MODEL slx_0a711875c262
CONFIG AbsTol = auto
CONFIG EnableMultiTasking = off
CONFIG FixedStep = 0.00001
CONFIG InitFcn = T = 0.0001;
VBUS = 311;

Ld = 0.00525;
Lq = 0.012;
Rs = 0.958;


Wc = 1000;
Ws = 8;

W_b = 2000;

CONFIG MaxStep = auto
CONFIG MinStep = auto
CONFIG RelTol = 1e-3
CONFIG SampleTimeConstraint = Unconstrained
CONFIG SolverName = FixedStepAuto
CONFIG StartTime = 0.0
CONFIG StopTime = 5
BLOCK [SubSystem] Anti_Park
BLOCK [Fcn] Anti_Park/Fcn
  Expr = cos(u[1])*u[2]-sin(u[1])*u[3]
BLOCK [Fcn] Anti_Park/Fcn1
  Expr = sin(u[1])*u[2]+cos(u[1])*u[3]
BLOCK [Mux] Anti_Park/Mux1
  DisplayOption = bar
  Inputs = 3
BLOCK [Outport] Anti_Park/Ualpha
BLOCK [Outport] Anti_Park/Ubeta
  Port = 2
BLOCK [Inport] Anti_Park/Vd
  Port = 2
BLOCK [Inport] Anti_Park/Vq
BLOCK [Inport] Anti_Park/angle
  Port = 3
BLOCK [SubSystem] CLARKE
BLOCK [Inport] CLARKE/A
BLOCK [Outport] CLARKE/Alpha
BLOCK [Inport] CLARKE/B
  Port = 2
BLOCK [Outport] CLARKE/Beta
  Port = 2
BLOCK [Inport] CLARKE/C
  Port = 3
BLOCK [Mux] CLARKE/Mux
  DisplayOption = bar
  Inputs = 3
BLOCK [Fcn] CLARKE/alpha
  Expr = (u(1)-0.5*(u(2)+u(3)))*2/3
BLOCK [Fcn] CLARKE/beta
  Expr = sqrt(3)/2*(u(2)-u(3))*2/3
BLOCK [Constant] Constant4
  Value = 0
BLOCK [Reference] DC  REF=spsDCVoltageSourceLib/DC Voltage Source
  LibrarySourceBlock = sps_lib/Sources/DC Voltage Source
  NameLocation = right
  SourceBlock = spsDCVoltageSourceLib/DC Voltage Source
  SourceType = DC Voltage Source
BLOCK [Demux] Demux
  Outputs = 3
BLOCK [From] From
  GotoTag = Them
  NameLocation = right
BLOCK [From] From1
  GotoTag = Wm
  NameLocation = right
BLOCK [From] From2
  GotoTag = Them
  NameLocation = top
BLOCK [From] From3
  GotoTag = Rad
  NameLocation = top
BLOCK [Gain] Gain
  Gain = 4
BLOCK [Goto] Goto
  GotoTag = Signal
BLOCK [Goto] Goto1
  GotoTag = Te
BLOCK [Goto] Goto2
  GotoTag = Them
BLOCK [Goto] Goto3
  GotoTag = Wm
BLOCK [Goto] Goto4
  GotoTag = Ialpha
BLOCK [Goto] Goto5
  GotoTag = Ibeta
BLOCK [Goto] Goto6
  GotoTag = Rad
BLOCK [Reference] Iq  REF=powerlib_extras/Discrete 
Control Blocks/Discrete
PI Controller
  NameLocation = top
  SourceBlock = powerlib_extras/Discrete 
Control Blocks/Discrete
PI Controller
  SourceType = Discrete PI Controller
BLOCK [SubSystem] Mux1
BLOCK [BusSelector] Mux1/Bus Selector
  OutputSignals = Stator current is_a (A),Stator current is_b (A),Stator current is_c (A)
BLOCK [BusSelector] Mux1/Bus Selector1
  OutputSignals = Rotor speed wm (rad/s),Rotor angle thetam (rad),Electromagnetic torque Te (N*m)
BLOCK [Outport] Mux1/Iabc
  Port = 3
BLOCK [Mux] Mux1/Mux
  DisplayOption = bar
  Inputs = 3
BLOCK [Outport] Mux1/Te
BLOCK [Outport] Mux1/Them
  Port = 2
BLOCK [Outport] Mux1/Wm
  Port = 4
BLOCK [Inport] Mux1/m
BLOCK [SubSystem] PARK
BLOCK [Inport] PARK/Alpha
BLOCK [Inport] PARK/Beta
  Port = 2
BLOCK [Outport] PARK/D
BLOCK [Mux] PARK/Mux
  DisplayOption = bar
  Inputs = 3
BLOCK [Outport] PARK/Q
  Port = 2
BLOCK [Inport] PARK/The
  Port = 3
BLOCK [Fcn] PARK/d
  Expr = u(1)*cos(u(3))+u(2)*sin(u(3))
BLOCK [Fcn] PARK/q
  Expr = -u(1)*sin(u(3))+u(2)*cos(u(3))
BLOCK [Reference] Permanent Magnet Synchronous Machine1  REF=spsPermanentMagnetSynchronousMachineLib/Permanent Magnet
Synchronous Machine
  SourceBlock = spsPermanentMagnetSynchronousMachineLib/Permanent Magnet
Synchronous Machine
  SourceType = Permanent Magnet Synchronous Machine
BLOCK [SubSystem] SVPWM
BLOCK [CCaller] SVPWM/C Caller
  FunctionName = SVPWM
  PortSpecificationStruct = %)30     .    8 H   8    (     @         %    "     8    !     0         %  0 "0    $    _    07)G3F%M90  4&]R=$YA;64 4V-O<&4     26YD97@     5'EP90      4VEZ90      27-';&]B86P   X    P    !@    @    $          4    (     0    0    !         !  ! !60E53#@   #     &    "     0         !0    @    !    !     $         $  $ %9"55,.    .     8    (    !          %    "     $    %     0         0    !0...<+3154ch>
BLOCK [Constant] SVPWM/Constant2
  Value = VBUS
BLOCK [DataTypeConversion] SVPWM/Data Type Conversion
  OutDataTypeStr = double
  RndMeth = Floor
  SaturateOnIntegerOverflow = off
BLOCK [DataTypeConversion] SVPWM/Data Type Conversion1
  OutDataTypeStr = double
  RndMeth = Floor
  SaturateOnIntegerOverflow = off
BLOCK [DataTypeConversion] SVPWM/Data Type Conversion2
  OutDataTypeStr = double
  RndMeth = Floor
  SaturateOnIntegerOverflow = off
BLOCK [Logic] SVPWM/Logical Operator
  AllPortsSameDT = off
  Operator = NOT
  OutDataTypeStr = boolean
BLOCK [Logic] SVPWM/Logical Operator1
  AllPortsSameDT = off
  Operator = NOT
  OutDataTypeStr = boolean
BLOCK [Logic] SVPWM/Logical Operator2
  AllPortsSameDT = off
  Operator = NOT
  OutDataTypeStr = boolean
BLOCK [Mux] SVPWM/Mux
  DisplayOption = bar
  Inputs = 6
BLOCK [Reference] SVPWM/PWM Generator  REF=eePwmGenerator/PWM Generator
  LibrarySourceBlock = ee_sl_lib/Pulse Width
Modulation/PWM Generator
  SourceBlock = eePwmGenerator/PWM Generator
  SourceType = PWM Generator
BLOCK [Reference] SVPWM/PWM Generator1  REF=eePwmGenerator/PWM Generator
  LibrarySourceBlock = ee_sl_lib/Pulse Width
Modulation/PWM Generator
  SourceBlock = eePwmGenerator/PWM Generator
  SourceType = PWM Generator
BLOCK [Reference] SVPWM/PWM Generator2  REF=eePwmGenerator/PWM Generator
  LibrarySourceBlock = ee_sl_lib/Pulse Width
Modulation/PWM Generator
  SourceBlock = eePwmGenerator/PWM Generator
  SourceType = PWM Generator
BLOCK [Inport] SVPWM/Valpha
BLOCK [Inport] SVPWM/Vbeta
  Port = 2
BLOCK [ZeroOrderHold] SVPWM/Zero-Order Hold
  SampleTime = T
BLOCK [ZeroOrderHold] SVPWM/Zero-Order Hold1
  SampleTime = T
BLOCK [Outport] SVPWM/pulse
BLOCK [Scope] Scope
  ActiveDisplayYMaximum = 83.45959853190611
  ActiveDisplayYMinimum = 71.221659633413722
  ContainerLayout = {"WindowBounds":[213.33333333333326,149.33333333333326,1280,768],"gridDimensions":{"w":1,"h":1},"tileCount":1,"tileCoverage":1,"columnWeights":1,"rowWeights":1,"tileOccupancy":{}}
  Floating = off
  GraphicalSettings = {"Style":{"BackgroundColor":[0.12941176470588237,0.12941176470588237,0.12941176470588237],"AxesColor":[0.07058823529411765,0.07058823529411765,0.07058823529411765],"LabelsColor":[0.8509803921568627,0.8509803921568627,0.8509803921568627],"PreserveColors":false,"Visible":[true,true,true],"LineStyle":["-","-","-"],"LineWidth":[1.5,1.5,1.5],"BarWidth":[0.9,0.9,0.9],"LineColor":["auto","auto","auto"],"...<+2360ch>
  MultipleDisplayCache = [{"MaxYLimMag":432.50451314474628,"MaxYLimReal":83.45959853190611,"MinYLimMag":0,"MinYLimReal":71.221659633413722,"PlotAsMagnitudePhase":false,"ShowGrid":true,"ShowLegend":true,"Title":"%<SignalLabel>","YLabel":""}]
  NameLocation = right
  NumInputPorts = 3
  ScopeFrameLocation = window
  ShowLegend = on
  Visible = on
  WasSavedAsWebScope = on
  WindowPosition = [290.000000,171.000000,688.000000,501.000000,]
BLOCK [Scope] Scope1
  ActiveDisplayYMaximum = 56.919768702194638
  ActiveDisplayYMinimum = -56.765093426646764
  DataLoggingVariableName = ScopeData1
  Floating = off
  GraphicalSettings = {"Style":{"BackgroundColor":[0.12941176470588237,0.12941176470588237,0.12941176470588237],"AxesColor":[0.07058823529411765,0.07058823529411765,0.07058823529411765],"LabelsColor":[0.8509803921568627,0.8509803921568627,0.8509803921568627],"PreserveColors":false,"Visible":[true,true,true],"LineStyle":["-","-","-"],"LineWidth":[1.5,1.5,1.5],"BarWidth":[0.9,0.9,0.9],"LineColor":["auto","auto","auto"],"...<+2203ch>
  MultipleDisplayCache = [{"MaxYLimMag":56.919768702194638,"MaxYLimReal":56.919768702194638,"MinYLimMag":0,"MinYLimReal":-56.765093426646764,"PlotAsMagnitudePhase":false,"ShowGrid":true,"ShowLegend":false,"Title":"%<SignalLabel>","YLabel":""}]
  NumInputPorts = 3
  ScopeFrameLocation = window
  WasSavedAsWebScope = on
  WindowPosition = [420.000000,327.000000,560.000000,420.000000,]
BLOCK [Scope] Scope2
  ActiveDisplayYMaximum = 14.952214172172493
  ActiveDisplayYMinimum = -3.4308453898305751
  DataLoggingVariableName = ScopeData2
  Floating = off
  GraphicalSettings = {"Style":{"BackgroundColor":[0.12941176470588237,0.12941176470588237,0.12941176470588237],"AxesColor":[0.07058823529411765,0.07058823529411765,0.07058823529411765],"LabelsColor":[0.8509803921568627,0.8509803921568627,0.8509803921568627],"PreserveColors":false,"Visible":[true,true],"LineStyle":["-","-"],"LineWidth":[1.5,1.5],"BarWidth":[0.9,0.9],"LineColor":["auto","auto"],"LineFaceAlpha":[1,1],"Li...<+2100ch>
  MultipleDisplayCache = [{"MaxYLimMag":14.952214172172493,"MaxYLimReal":14.952214172172493,"MinYLimMag":0,"MinYLimReal":-3.4308453898305751,"PlotAsMagnitudePhase":false,"ShowGrid":true,"ShowLegend":false,"Title":"%<SignalLabel>","YLabel":""}]
  NumInputPorts = 2
  ScopeFrameLocation = window
  WasSavedAsWebScope = on
  WindowPosition = [420.000000,327.000000,560.000000,420.000000,]
BLOCK [Scope] Scope3
  ActiveDisplayYMaximum = 11.569758124701689
  ActiveDisplayYMinimum = -12.718687980408173
  ContainerLayout = {"WindowBounds":[213.33333333333326,149.33333333333326,1280,768],"gridDimensions":{"w":1,"h":1},"tileCount":1,"tileCoverage":1,"columnWeights":1,"rowWeights":1,"tileOccupancy":{}}
  DataLoggingVariableName = ScopeData3
  Floating = off
  GraphicalSettings = {"Style":{"BackgroundColor":[0.12941176470588237,0.12941176470588237,0.12941176470588237],"AxesColor":[0.07058823529411765,0.07058823529411765,0.07058823529411765],"LabelsColor":[0.8509803921568627,0.8509803921568627,0.8509803921568627],"PreserveColors":false,"Visible":[true,true],"LineStyle":["-","-"],"LineWidth":[1.5,1.5],"BarWidth":[0.9,0.9],"LineColor":["auto","auto"],"LineFaceAlpha":[1,1],"Li...<+2108ch>
  MultipleDisplayCache = [{"MaxYLimMag":16.784580665603098,"MaxYLimReal":11.569758124701689,"MinYLimMag":0,"MinYLimReal":-12.718687980408173,"PlotAsMagnitudePhase":false,"ShowGrid":true,"ShowLegend":true,"Title":"%<SignalLabel>","YLabel":""}]
  NumInputPorts = 2
  ScopeFrameLocation = window
  ShowLegend = on
  WasSavedAsWebScope = on
  WindowPosition = [577.000000,260.000000,560.000000,420.000000,]
BLOCK [Scope] Scope4
  ActiveDisplayYMaximum = 249.87801666414541
  ActiveDisplayYMinimum = -120.45590110912798
  ContainerLayout = {"WindowBounds":[213.33333333333326,149.33333333333326,1280,768],"gridDimensions":{"w":1,"h":1},"tileCount":1,"tileCoverage":1,"columnWeights":1,"rowWeights":1,"tileOccupancy":{}}
  DataLoggingVariableName = ScopeData4
  Floating = off
  GraphicalSettings = {"Style":{"BackgroundColor":[0.12941176470588237,0.12941176470588237,0.12941176470588237],"AxesColor":[0.07058823529411765,0.07058823529411765,0.07058823529411765],"LabelsColor":[0.8509803921568627,0.8509803921568627,0.8509803921568627],"PreserveColors":false,"Visible":[true,true],"LineStyle":["-","-"],"LineWidth":[1.5,1.5],"BarWidth":[0.9,0.9],"LineColor":["auto","auto"],"LineFaceAlpha":[1,1],"Li...<+2090ch>
  MultipleDisplayCache = [{"MaxYLimMag":15.588457268119896,"MaxYLimReal":249.87801666414541,"MinYLimMag":0,"MinYLimReal":-120.45590110912798,"PlotAsMagnitudePhase":false,"ShowGrid":true,"ShowLegend":true,"Title":"%<SignalLabel>","YLabel":""}]
  NumInputPorts = 2
  ScopeFrameLocation = window
  ShowLegend = on
  WasSavedAsWebScope = on
  WindowPosition = [696.000000,322.000000,560.000000,420.000000,]
BLOCK [Scope] Scope5
  ActiveDisplayYMaximum = 0.38689833522072209
  ActiveDisplayYMinimum = -2.417785617585527
  DataLoggingVariableName = ScopeData5
  Floating = off
  GraphicalSettings = {"Style":{"BackgroundColor":[0.12941176470588237,0.12941176470588237,0.12941176470588237],"AxesColor":[0.07058823529411765,0.07058823529411765,0.07058823529411765],"LabelsColor":[0.8509803921568627,0.8509803921568627,0.8509803921568627],"PreserveColors":false,"Visible":[true],"LineStyle":["-"],"LineWidth":[1.5],"BarWidth":[0.9],"LineColor":["auto"],"LineFaceAlpha":[1],"LineEdgeAlpha":[1],"Marker":...<+1895ch>
  MultipleDisplayCache = [{"MaxYLimMag":2.417785617585527,"MaxYLimReal":0.38689833522072209,"MinYLimMag":0,"MinYLimReal":-2.417785617585527,"PlotAsMagnitudePhase":false,"ShowGrid":true,"ShowLegend":false,"Title":"%<SignalLabel>","YLabel":""}]
  NumInputPorts = 1
  ScopeFrameLocation = window
  WasSavedAsWebScope = on
  WindowPosition = [573.000000,323.000000,560.000000,420.000000,]
BLOCK [Scope] Scope6
  ActiveDisplayYMaximum = 1828.1288182778874
  ActiveDisplayYMinimum = -6.298375426201801
  DataLoggingVariableName = ScopeData6
  Floating = off
  GraphicalSettings = {"AxesScalingProperties":{"AlignXAxis":"Center","AlignYAxis":"Center","AutoScaleXAxisLimits":false,"AxesScaling":"Manual","AxesScalingNumUpdates":10,"ExpandOnly":true,"ScaleAxesLimitsAtStop":false,"XAxisDataRange":100,"YAxisDataRange":80},"DisplayProperties":{"ColorOrder":["auto","auto","auto","auto","auto","auto","auto","auto","auto","auto","auto","auto","auto","auto","auto","auto","auto","auto",...<+2117ch>
  MultipleDisplayCache = [{"MaxYLimMag":1419.1346246899052,"MaxYLimReal":1828.1288182778874,"MinYLimMag":0,"MinYLimReal":-6.298375426201801,"PlotAsMagnitudePhase":false,"ShowGrid":true,"ShowLegend":true,"Title":"%<SignalLabel>","YLabel":""}]
  NumInputPorts = 2
  ScopeFrameLocation = window
  ShowLegend = on
  WasSavedAsWebScope = on
  WindowPosition = [656.000000,258.000000,560.000000,420.000000,]
BLOCK [Scope] Scope7
  ActiveDisplayYMaximum = 20.129691037464234
  ActiveDisplayYMinimum = 3.84321816794486
  DataLoggingVariableName = ScopeData7
  Floating = off
  GraphicalSettings = {"AxesScalingProperties":{"AlignXAxis":"Center","AlignYAxis":"Center","AutoScaleXAxisLimits":false,"AxesScaling":"Manual","AxesScalingNumUpdates":10,"ExpandOnly":true,"ScaleAxesLimitsAtStop":false,"XAxisDataRange":100,"YAxisDataRange":80},"DisplayProperties":{"ColorOrder":["auto","auto","auto","auto","auto","auto","auto","auto","auto","auto","auto","auto","auto","auto","auto","auto","auto","auto",...<+2119ch>
  MultipleDisplayCache = [{"MaxYLimMag":22.5,"MaxYLimReal":20.129691037464234,"MinYLimMag":0,"MinYLimReal":3.84321816794486,"PlotAsMagnitudePhase":false,"ShowGrid":true,"ShowLegend":true,"Title":"%<SignalLabel>","YLabel":""}]
  NumInputPorts = 2
  ScopeFrameLocation = window
  ShowLegend = on
  WasSavedAsWebScope = on
  WindowPosition = [656.000000,258.000000,560.000000,420.000000,]
BLOCK [Sum] Sum
  Inputs = |+-
BLOCK [Sum] Sum1
  Inputs = |+-
BLOCK [Sum] Sum2
  Inputs = |+-
BLOCK [Sum] Sum3
  Inputs = |+-
BLOCK [Step] TL
  SampleTime = 0
  Time = 3
BLOCK [SubSystem] Theta_Signal
BLOCK [Sum] Theta_Signal/Add
  IconShape = rectangular
BLOCK [Constant] Theta_Signal/Constant3
BLOCK [Gain] Theta_Signal/Gain
  Gain = pi
BLOCK [Reference] Theta_Signal/Sawtooth Generator  REF=spsSawtoothGeneratorLib/Sawtooth
Generator
  LibrarySourceBlock = sps_lib/Sources/Signal Generator Sources/Sawtooth
Generator
  SourceBlock = spsSawtoothGeneratorLib/Sawtooth
Generator
  SourceType = Sawtooth Generator
BLOCK [Outport] Theta_Signal/angle
BLOCK [TransferFcn] Transfer Fcn2
  Denominator = [1 sqrt(2)*Wc Wc^2]
  NameLocation = top
  Numerator = [Wc^2]
BLOCK [ZeroOrderHold] Zero-Order Hold
  NameLocation = right
  SampleTime = 0.0001
BLOCK [Reference] inverter  REF=spsUniversalBridgeLib/Universal Bridge
  LibrarySourceBlock = sps_lib/Power Electronics/Universal Bridge
  NameLocation = top
  SourceBlock = spsUniversalBridgeLib/Universal Bridge
  SourceType = Universal Bridge
BLOCK [Reference] ld  REF=powerlib_extras/Discrete 
Control Blocks/Discrete
PI Controller
  NameLocation = top
  SourceBlock = powerlib_extras/Discrete 
Control Blocks/Discrete
PI Controller
  SourceType = Discrete PI Controller
BLOCK [SubSystem] pi-Iq2
  AncestorBlock = powerlib_extras/Discrete 
Control Blocks/Discrete
PI Controller
  DialogController = POWERSYS.PowerSysDialog
BLOCK [DiscreteIntegrator] pi-Iq2/Discrete-Time Integrator
  ICPrevOutput = DiscIntNeverNeededParam
  ICPrevScaledInput = DiscIntNeverNeededParam
  InitialCondition = Init
  LimitOutput = on
  LowerSaturationLimit = LowerLimit
  SampleTime = Ts
  UpperSaturationLimit = UpperLimit
BLOCK [Inport] pi-Iq2/Error
  SampleTime = Ts
BLOCK [Gain] pi-Iq2/Kp4
  Gain = Kp
  OutDataTypeStr = Inherit: Same as input
  ParamDataTypeStr = Inherit: Same as input
  SampleTime = Ts
  SaturateOnIntegerOverflow = on
BLOCK [Gain] pi-Iq2/Kp5
  Gain = Ki
  OutDataTypeStr = Inherit: Same as input
  ParamDataTypeStr = Inherit: Same as input
  SampleTime = Ts
  SaturateOnIntegerOverflow = on
BLOCK [Outport] pi-Iq2/Out
  InitialOutput = 0
  SampleTime = Ts
BLOCK [Saturate] pi-Iq2/Saturation2
  LowerLimit = LowerLimit
  NameLocation = top
  SampleTime = Ts
  UpperLimit = UpperLimit
BLOCK [Sum] pi-Iq2/Sum6
  IconShape = rectangular
  InputSameDT = on
  OutDataTypeStr = Inherit: Same as first input
  SampleTime = Ts
  SaturateOnIntegerOverflow = on
BLOCK [ZeroOrderHold] pi-Iq2/Zero-Order Hold
  SampleTime = Ts
BLOCK [Reference] powergui  REF=spspowerguiLib/powergui
  SourceBlock = spspowerguiLib/powergui
  SourceType = PSB option menu block
BLOCK [Step] set
  After = 20
  NameLocation = top
  SampleTime = 0
  Time = 2
BLOCK [SubSystem] velocity1
  AncestorBlock = powerlib_extras/Discrete 
Control Blocks/Discrete
PI Controller
  DialogController = POWERSYS.PowerSysDialog
BLOCK [DiscreteIntegrator] velocity1/Discrete-Time Integrator
  ICPrevOutput = DiscIntNeverNeededParam
  ICPrevScaledInput = DiscIntNeverNeededParam
  InitialCondition = Init
  LimitOutput = on
  LowerSaturationLimit = LowerLimit
  SampleTime = Ts
  UpperSaturationLimit = UpperLimit
BLOCK [Inport] velocity1/Error
  SampleTime = Ts
BLOCK [Gain] velocity1/Kp4
  Gain = Kp
  OutDataTypeStr = Inherit: Same as input
  ParamDataTypeStr = Inherit: Same as input
  SampleTime = Ts
  SaturateOnIntegerOverflow = on
BLOCK [Gain] velocity1/Kp5
  Gain = Ki
  OutDataTypeStr = Inherit: Same as input
  ParamDataTypeStr = Inherit: Same as input
  SampleTime = Ts
  SaturateOnIntegerOverflow = on
BLOCK [Outport] velocity1/Out
  InitialOutput = 0
  SampleTime = Ts
BLOCK [Saturate] velocity1/Saturation2
  LowerLimit = LowerLimit
  NameLocation = top
  SampleTime = Ts
  UpperLimit = UpperLimit
BLOCK [Sum] velocity1/Sum6
  IconShape = rectangular
  InputSameDT = on
  OutDataTypeStr = Inherit: Same as first input
  SampleTime = Ts
  SaturateOnIntegerOverflow = on
BLOCK [ZeroOrderHold] velocity1/Zero-Order Hold
  SampleTime = Ts
BLOCK [Gain] wm->Nr
  Gain = 30/pi
  NameLocation = right
LINE Anti_Park/Fcn1:1 -> Anti_Park/Ubeta:1
LINE Anti_Park/Fcn:1 -> Anti_Park/Ualpha:1
LINE Anti_Park/Mux1:1 -> Anti_Park/Fcn1:1
LINE Anti_Park/Mux1:1 -> Anti_Park/Fcn:1
LINE Anti_Park/Vd:1 -> Anti_Park/Mux1:2
LINE Anti_Park/Vq:1 -> Anti_Park/Mux1:3
LINE Anti_Park/angle:1 -> Anti_Park/Mux1:1
LINE Anti_Park:1 -> SVPWM:1
LINE Anti_Park:2 -> SVPWM:2
LINE CLARKE/A:1 -> CLARKE/Mux:1
LINE CLARKE/B:1 -> CLARKE/Mux:2
LINE CLARKE/C:1 -> CLARKE/Mux:3
LINE CLARKE/Mux:1 -> CLARKE/alpha:1
LINE CLARKE/Mux:1 -> CLARKE/beta:1
LINE CLARKE/alpha:1 -> CLARKE/Alpha:1
LINE CLARKE/beta:1 -> CLARKE/Beta:1
LINE CLARKE:1 -> Goto4:1
LINE CLARKE:1 -> PARK:1
LINE CLARKE:1 -> Scope2:1
LINE CLARKE:2 -> Goto5:1
LINE CLARKE:2 -> PARK:2
LINE CLARKE:2 -> Scope2:2
LINE Constant4:1 -> Sum1:1
LINE DC:lconn -> inverter:rconn
LINE DC:rconn -> inverter:rconn
LINE Demux:1 -> CLARKE:1
LINE Demux:1 -> Scope1:1
LINE Demux:2 -> CLARKE:2
LINE Demux:2 -> Scope1:2
LINE Demux:3 -> CLARKE:3
LINE Demux:3 -> Scope1:3
LINE From1:1 -> wm->Nr:1
LINE From2:1 -> Anti_Park:3
LINE From2:1 -> Scope5:1
LINE From3:1 -> Scope7:2
LINE From3:1 -> Sum3:2
LINE From:1 -> PARK:3
LINE Gain:1 -> Goto2:1
LINE Iq:1 -> Anti_Park:1
LINE Iq:1 -> Scope4:1
LINE Mux1/Bus Selector1:1 -> Mux1/Wm:1
LINE Mux1/Bus Selector1:2 -> Mux1/Them:1
LINE Mux1/Bus Selector1:3 -> Mux1/Te:1
LINE Mux1/Bus Selector:1 -> Mux1/Mux:1
LINE Mux1/Bus Selector:2 -> Mux1/Mux:2
LINE Mux1/Bus Selector:3 -> Mux1/Mux:3
LINE Mux1/Mux:1 -> Mux1/Iabc:1
LINE Mux1/m:1 -> Mux1/Bus Selector1:1
LINE Mux1/m:1 -> Mux1/Bus Selector:1
LINE Mux1:1 -> Goto1:1
LINE Mux1:1 -> Scope:1
LINE Mux1:2 -> Gain:1
LINE Mux1:2 -> Goto6:1
LINE Mux1:2 -> Scope:2
LINE Mux1:3 -> Zero-Order Hold:1
LINE Mux1:4 -> Goto3:1
LINE Mux1:4 -> Scope:3
LINE PARK/Alpha:1 -> PARK/Mux:1
LINE PARK/Beta:1 -> PARK/Mux:2
LINE PARK/Mux:1 -> PARK/d:1
LINE PARK/Mux:1 -> PARK/q:1
LINE PARK/The:1 -> PARK/Mux:3
LINE PARK/d:1 -> PARK/D:1
LINE PARK/q:1 -> PARK/Q:1
LINE PARK:1 -> Scope3:1
LINE PARK:1 -> Sum1:2
LINE PARK:2 -> Scope3:2
LINE PARK:2 -> Sum:2
LINE Permanent Magnet Synchronous Machine1:1 -> Mux1:1
LINE Permanent Magnet Synchronous Machine1:lconn -> inverter:lconn
LINE Permanent Magnet Synchronous Machine1:lconn -> inverter:lconn
LINE SVPWM/C Caller:1 -> SVPWM/PWM Generator:1
LINE SVPWM/C Caller:2 -> SVPWM/PWM Generator1:1
LINE SVPWM/C Caller:3 -> SVPWM/PWM Generator2:1
LINE SVPWM/Constant2:1 -> SVPWM/C Caller:1
LINE SVPWM/Data Type Conversion1:1 -> SVPWM/Mux:4
LINE SVPWM/Data Type Conversion2:1 -> SVPWM/Mux:6
LINE SVPWM/Data Type Conversion:1 -> SVPWM/Mux:2
LINE SVPWM/Logical Operator1:1 -> SVPWM/Data Type Conversion1:1
LINE SVPWM/Logical Operator2:1 -> SVPWM/Data Type Conversion2:1
LINE SVPWM/Logical Operator:1 -> SVPWM/Data Type Conversion:1
LINE SVPWM/Mux:1 -> SVPWM/pulse:1
LINE SVPWM/PWM Generator1:1 -> SVPWM/Logical Operator1:1
LINE SVPWM/PWM Generator1:1 -> SVPWM/Mux:3
LINE SVPWM/PWM Generator2:1 -> SVPWM/Logical Operator2:1
LINE SVPWM/PWM Generator2:1 -> SVPWM/Mux:5
LINE SVPWM/PWM Generator:1 -> SVPWM/Logical Operator:1
LINE SVPWM/PWM Generator:1 -> SVPWM/Mux:1
LINE SVPWM/Valpha:1 -> SVPWM/Zero-Order Hold1:1
LINE SVPWM/Vbeta:1 -> SVPWM/Zero-Order Hold:1
LINE SVPWM/Zero-Order Hold1:1 -> SVPWM/C Caller:2
LINE SVPWM/Zero-Order Hold:1 -> SVPWM/C Caller:3
LINE SVPWM:1 -> inverter:1
LINE Sum1:1 -> ld:1
LINE Sum2:1 -> velocity1:1
LINE Sum3:1 -> pi-Iq2:1
LINE Sum:1 -> Iq:1
LINE TL:1 -> Permanent Magnet Synchronous Machine1:1
LINE Theta_Signal/Add:1 -> Theta_Signal/Gain:1
LINE Theta_Signal/Constant3:1 -> Theta_Signal/Add:2
LINE Theta_Signal/Gain:1 -> Theta_Signal/angle:1
LINE Theta_Signal/Sawtooth Generator:1 -> Theta_Signal/Add:1
LINE Theta_Signal:1 -> Goto:1
LINE Zero-Order Hold:1 -> Demux:1
LINE inverter:lconn -> Permanent Magnet Synchronous Machine1:lconn
LINE ld:1 -> Anti_Park:2
LINE ld:1 -> Scope4:2
LINE pi-Iq2:1 -> Scope6:1
LINE pi-Iq2:1 -> Sum2:1
LINE set:1 -> Scope7:1
LINE set:1 -> Sum3:1
LINE velocity1:1 -> Sum:1
LINE wm->Nr:1 -> Scope6:2
LINE wm->Nr:1 -> Sum2:2
